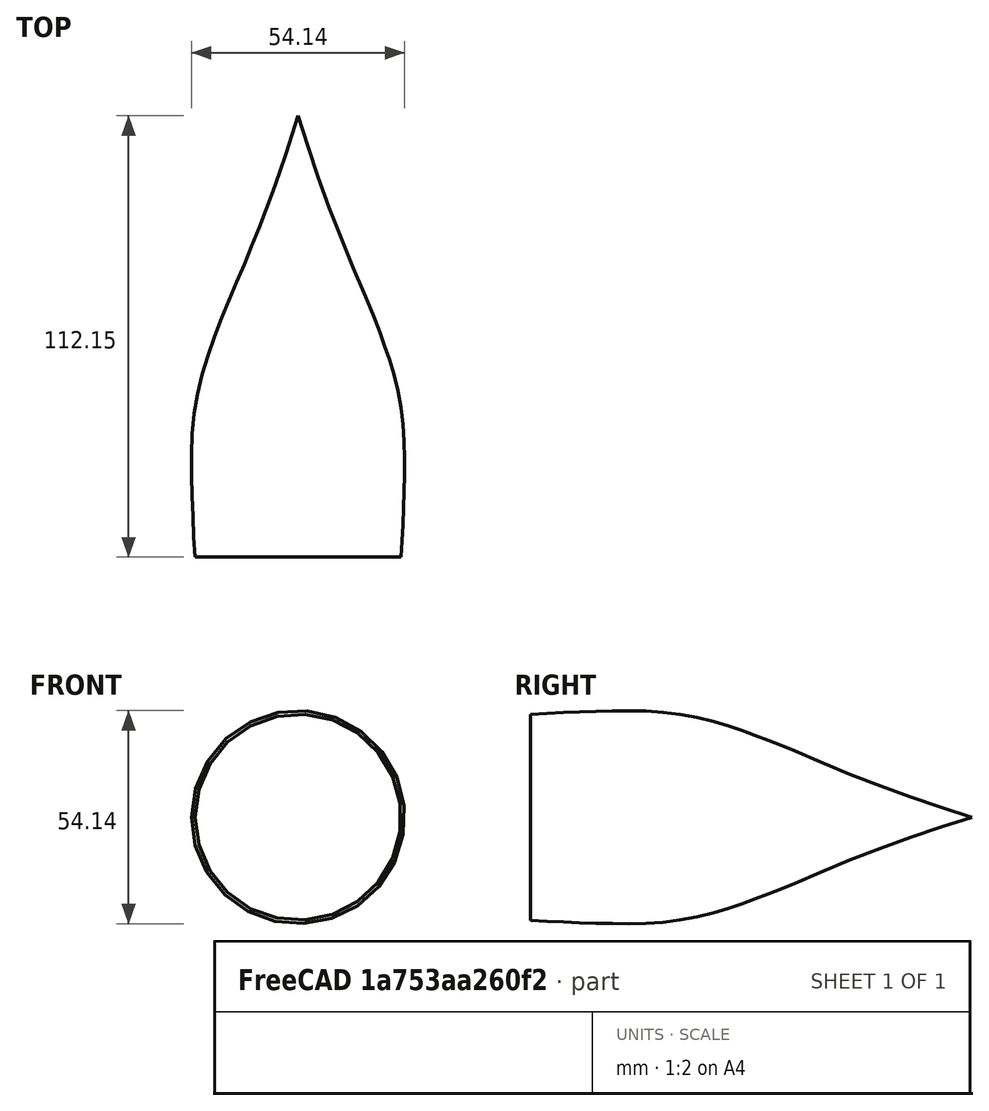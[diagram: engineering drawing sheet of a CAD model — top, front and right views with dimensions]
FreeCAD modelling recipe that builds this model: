
FCSTD DOCUMENT  (FreeCAD 0.20R29177 +426 (Git))
Label: project_7
License: All rights reserved
LicenseURL: https://en.wikipedia.org/wiki/All_rights_reserved
objects: Part::FeaturePython×5, Sketcher::SketchObject×2, Part::Revolution×1, App::DocumentObjectGroup×1, Part::Loft×1
note: 9 computed .brp shape members not serialized (recipe doc carries the construction recipe); baked Part::Feature solids carry a one-line shape summary decoded from their .brp

FEATURE [Sketcher::SketchObject] Sketch
  FullyConstrained = false
  sketch-geometry (5):
    g0: GeomPoint X=-14.8298 Y=37.9254 Z=0
    g1: GeomPoint X=-20.0162 Y=25.4457 Z=0
    g2: GeomPoint X=-25.3647 Y=8.42788 Z=0
    g3: GeomPoint X=-26.9854 Y=-14.7488 Z=0
    g4: GeomPoint X=-26.175 Y=-33.7115 Z=0
FEATURE [Part::Revolution] Revolve
  Angle = 360
  Axis = (0,1,0)
  Base = (0,0,0)
  FaceMakerClass = Part::FaceMakerBullseye
  Solid = false
  Source = -> Sketch
  Symmetric = false
FEATURE [Sketcher::SketchObject] Sketch001
  FullyConstrained = false
  Placement = pos=(0,0,0) rot=(0.57735,0.57735,0.57735;2.0944rad)
  sketch-geometry (1):
    g0: GeomPoint X=78.441 Y=0 Z=0
  constraints (1):
    c: PointOnObject(g0,g-1)
FEATURE [Part::FeaturePython] Revolve_child0  label="Revolve.0"  # WARN: FeaturePython — macro-defined, semantics opaque (R4)
  Base = -> Revolve
  FilterType = 1
  Invert = false
  OverrideMaxVal = 0
  WindowFrom = 80
  WindowTo = 100
  items = 0
FEATURE [Part::FeaturePython] Revolve_child1  label="Revolve.1"  # WARN: FeaturePython — macro-defined, semantics opaque (R4)
  Base = -> Revolve
  FilterType = 1
  Invert = false
  OverrideMaxVal = 0
  WindowFrom = 80
  WindowTo = 100
  items = 1
FEATURE [Part::FeaturePython] Revolve_child2  label="Revolve.2"  # WARN: FeaturePython — macro-defined, semantics opaque (R4)
  Base = -> Revolve
  FilterType = 1
  Invert = false
  OverrideMaxVal = 0
  WindowFrom = 80
  WindowTo = 100
  items = 2
FEATURE [Part::FeaturePython] Revolve_child3  label="Revolve.3"  # WARN: FeaturePython — macro-defined, semantics opaque (R4)
  Base = -> Revolve
  FilterType = 1
  Invert = false
  OverrideMaxVal = 0
  WindowFrom = 80
  WindowTo = 100
  items = 3
FEATURE [Part::FeaturePython] Revolve_child4  label="Revolve.4"  # WARN: FeaturePython — macro-defined, semantics opaque (R4)
  Base = -> Revolve
  FilterType = 1
  Invert = false
  OverrideMaxVal = 0
  WindowFrom = 80
  WindowTo = 100
  items = 4
FEATURE [App::DocumentObjectGroup] GrExplode_Revolve  label="Exploded Revolve"
  Group = -> [Revolve_child0,Revolve_child1,Revolve_child2,Revolve_child3,Revolve_child4]
FEATURE [Part::Loft] Loft
  Closed = false
  MaxDegree = 2
  Ruled = false
  Sections = -> [Sketch001,Revolve_child0,Revolve_child1,Revolve_child2,Revolve_child3,Revolve_child4]
  Solid = false
